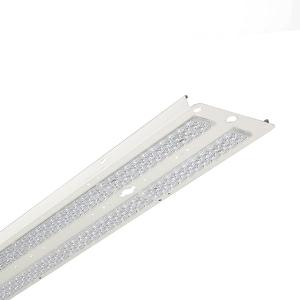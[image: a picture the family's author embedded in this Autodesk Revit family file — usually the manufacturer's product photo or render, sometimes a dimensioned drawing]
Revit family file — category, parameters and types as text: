
# Revit family: 3f_filippi_-_kit_led_retrofit_per_schermo_in_vetro_3f_filippi_-_a5212_a5184_-_kit_led_i3f_76_a3f_91_-_l1_8792eeac05144c52
name_source: partatom
category: Lighting Fixtures
units: mm (PartAtom-declared; Revit-internal decimal feet)

## family parameters
Cut with Voids When Loaded = No
Host = Face
Light Source = No
Part Type = Normal
Room Calculation Point = No
Round Connector Dimension = Use Diameter
Shared = No

## types (1)
- 3F Filippi - Kit LED Retrofit per schermo in vetro (1 x LED, 10049 lm, 74 W, 4000 K)
    Apparent Load = 74 VA
    Approval mark = ENEC
    CIE Flux Codes = 75 93 98 100 100
    Color Rendering = 80
    Color Temperature = 4000 K
    Control Gear = Electronic ballast
    Default Elevation = 1800 mm
    Description = Led retrofit kit suitable for Fluorescent Beta 2x i3F 76 and A3F 91 luminaires.

ILLUMINOTECHNICAL
Luminous efficiency 100% (DLOR 100%, ULOR 0%).
Initial luminous flux of the luminaire 10049 lm.
Symmetric concentrated distribution.
Installation Interdistance Transv.D = 0.61 x hu - Long.D = 0.93 x hu.
Tabular UGR (CIE 117 - 4H-8H; S=0.25H; 70/50/20): RUG 17.7 - 19.8.
Beam angle: 39° - 63°.
Luminous efficacy 136 lm/W.
Lifetime (L93/B10): 30000 h. (tq+25°C)
Lifetime (L90/B10): 50000 h. (tq+25°C)
Lifetime (L85/B10): 80000 h. (tq+25°C)
Lifetime (L80/B10): 100000 h. (tq+25°C)
Lifetime (L85/B10): 50000 h. (tq+40°C)
Sudden decreased luminous flux after 50000 hours: 0% (C0).
Photobiological safety in compliance with IEC/TR 62778: RG0 risk exempt, (IEC 62471).
In compliance with IEC/EN 62722-2-1 - IEC/EN 62717 standards.

SOURCE
2 linear LED modules 40W/840.
Energy efficiency class (UE 2019/2020 - UE 2019/2015): C.
CIE 13.3 Colour rendering index: CRI >80 (R9 <50%).
IES TM-30 Fidelity Index: Rf = 84 Rg = 95.
CCT nominal colour temperature 4000 K.
Colour initial tolerance (MacAdam): SDCM 3.

MECHANICAL
Gear-tray unit in hot-galvanised steel, painted in white polyester, fixed to the housing by means of "Ribloc" rapid devices in galvanised steel, hinged opening.
Transparent methacrylate (PMMA) concentrated distribution lenses with flat external surface.
Luminaire with limited surface temperature. - D - (EN 60598-2-24)
Dimensions: 1565x235 mm, height 105 mm. Weight 7.912 kg.
Glow-wire test resistance 850°C.

ELECTRICAL
Halogen Free electronic wiring 230V-50/60Hz, power factor 0.95, THD <25%, constant output current, class I, 1 driver.
Power of the luminaire 74 W.
CE - IEC 60598-1 - EN 60598-1.
SAFE FLICKER: PstLM=<1 and SVM=<0.4 (IEC TR 61547-1 and IEC TR 63158), to ensure a more comfortable and safe light.
Luminaire compliant with EN 60598-2-22 for power supply from a centralised emergency system CPSS (Central Power Supply System), not incorporated in the luminaire - high risk areas excluded. The default power and flux are 100% in AC and 100% in DC.
Ambient temperature from -20°C to +40°C.
Temperature class T6 max 85°C.
Relative humidity UR: <85%.

INSTALLATION
Retrofit.
Correct installation of the retrofit LED kit, compliant with EN 60598-1 and CE marked, inside the 3F Filippi - Beta 2x i3F 76 and A3F 91 Fluorescent luminaires must be only carried out by qualified personnel to ensure compliance with the national installation standards.
Attention: to maintain the degree of protection of the device and for the purposes of validity of the guarantee of the new retrofit kits, it is imperative to replace the old cable guides (on the body of the device) with the new ones supplied.
All accessories dedicated to this product are available on the Catalog and on our website www.3F-Filippi.com.

ACCESSORIES
A5184 - Printed glass Beta 2x i3F 76 - L1565.

WARNING
Fixture not suitable for cold stores with an ambient temperature <0°C and/or relative humidity >85%.
Luminaire designed for disposal/recycling at end-of-life.
Replaceable (LED only) light source by a professional. Replaceable control gear by a professional.
    Height = 105 mm
    Lamp = 1 x LED
    Lamp Light Flux = 10049 lm
    Lamp Power = 74 W
    Lamp count = 1
    Length = 1565 mm
    Lifetime = 50000 h
    Luminous efficacy = 136 lm/W
    Manufacturer = 3F Filippi
    ModVariant = No
    Model = 3F Filippi - A5212+A5184 - Kit LED i3F 76,A3F 91 - L1565 - L 2x40W CONC + VS
    Mounting Place = Ceiling
    Mounting Type = Surface mounted
    Number of Poles = 1
    OnlyDefault = Yes
    Power Factor = 1
    Product Name = 3F Filippi - Kit LED Retrofit per schermo in vetro
    Product group = ceiling mounted luminaire
    ProductGroupID = 3
    Protection Class = Protection class I
    Protection Degree = Degree of protection
    RLX_Detail_Level = 1
    RLX_Emergency_Light_Flux = 0 lm
    RLX_Emergency_Type = 0
    RLX_Emergency_Type_DB = No
    RlxData = <blob elided: 69977 chars, md5=f9187596>
    Socket = socket
    Standby Power = 0 W
    System Light Flux = 10049 lm
    System Power = 74 W
    Type Comments = Product without accessories
    Type Image = 3ffilippi_a5212_a5184.jpg
    URL = http://relux.com
    VarID = ---
    Voltage = 0 V
    Weight = 0.00 kg
    Width = 235 mm

## geometry (parser evidence)
native form markers: Blend x4, Sweep x10
no freeform markers — native parametric forms only
